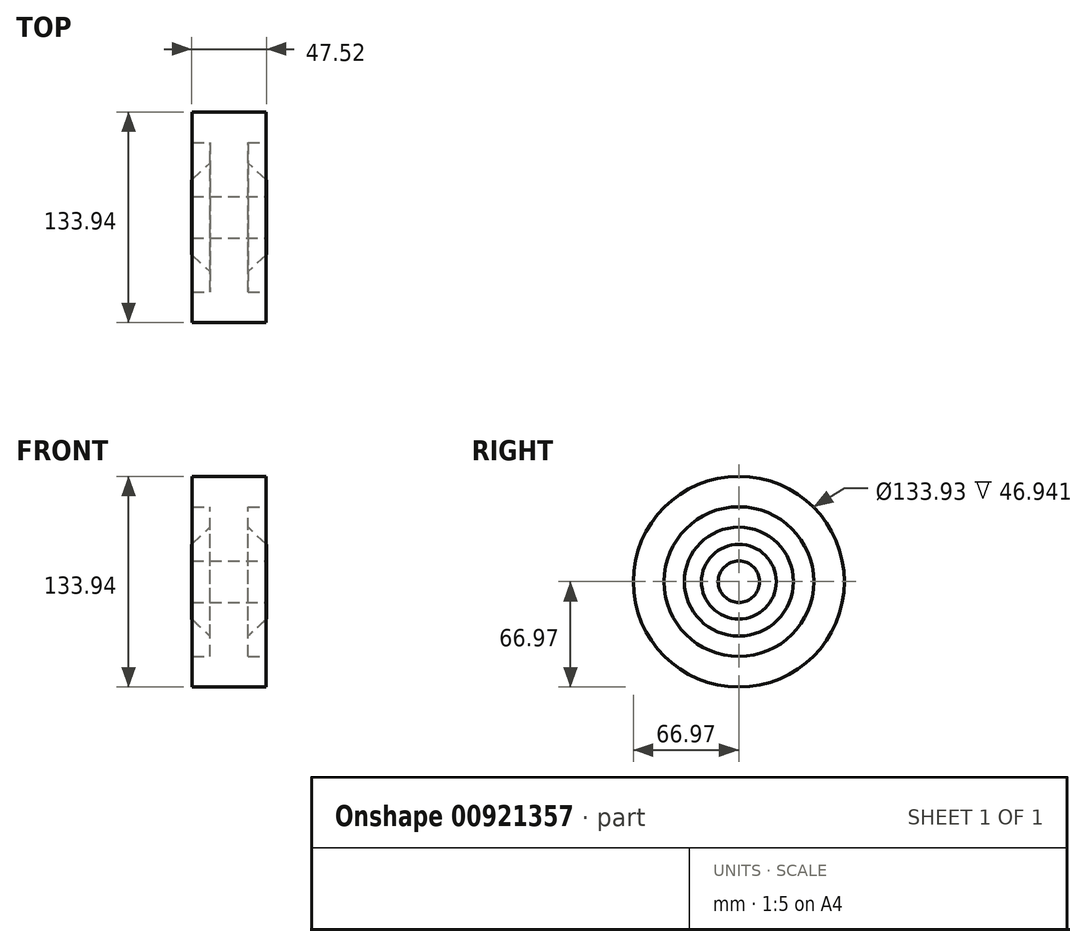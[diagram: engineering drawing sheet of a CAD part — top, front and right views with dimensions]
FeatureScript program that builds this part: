
annotation { "Feature Type Name" : "Feature", "Feature Type Description" : "" }
export const myFeature = defineFeature(function(context is Context, id is Id, definition is map)
    precondition{}
    {
        {
            var Q0;
            Q0=qCreatedBy(makeId("Front.planeOp"),FACE);
            var sketch = newSketch(context, id + "F0", { "sketchPlane" : qUnion([Q0])});
            skLineSegment(sketch, "E0", {"start": v(-23.47, 47.55) * mm, "end": v(-23.47, 66.97) * mm});
            skLineSegment(sketch, "E1", {"start": v(-23.47, 66.97) * mm, "end": v(0, 66.97) * mm});
            skLineSegment(sketch, "E2", {"start": v(-12, 47.55) * mm, "end": v(-23.47, 47.55) * mm});
            skLineSegment(sketch, "E3", {"start": v(-12, 34.6) * mm, "end": v(-12, 47.55) * mm});
            skLineSegment(sketch, "E4", {"start": v(-23.76, 23.72) * mm, "end": v(-12, 34.6) * mm});
            skLineSegment(sketch, "E5", {"start": v(-23.76, 13.13) * mm, "end": v(-23.76, 23.72) * mm});
            skLineSegment(sketch, "E6", {"start": v(0, 13.13) * mm, "end": v(-23.76, 13.13) * mm});
            skLineSegment(sketch, "E7", {"start": v(-44.36, 0) * mm, "end": v(42.73, 0) * mm});
            skLineSegment(sketch, "E8.MirrorCS", {"start": v(23.47, 66.97) * mm, "end": v(0, 66.97) * mm});
            skLineSegment(sketch, "E9.MirrorCS", {"start": v(23.47, 47.55) * mm, "end": v(23.47, 66.97) * mm});
            skLineSegment(sketch, "E10.MirrorCS", {"start": v(12, 47.55) * mm, "end": v(23.47, 47.55) * mm});
            skLineSegment(sketch, "E11.MirrorCS", {"start": v(12, 34.6) * mm, "end": v(12, 47.55) * mm});
            skLineSegment(sketch, "E12.MirrorCS", {"start": v(23.76, 23.72) * mm, "end": v(12, 34.6) * mm});
            skLineSegment(sketch, "E13.MirrorCS", {"start": v(23.76, 13.13) * mm, "end": v(23.76, 23.72) * mm});
            skLineSegment(sketch, "E14.MirrorCS", {"start": v(0, 13.13) * mm, "end": v(23.76, 13.13) * mm});
            skSolve(sketch);
        }
        {
            var Q0;
            Q0 = qSketchRegion(id + "F0", true);
            var Q1;
            Q1=sQuery(id+"F0.wireOp",EDGE,"E3");
            var Q2;
            Q2=sQuery(id+"F0.wireOp",EDGE,"E2");
            var Q3;
            Q3=sQuery(id+"F0.wireOp",EDGE,"E0");
            var Q4;
            Q4=sQuery(id+"F0.wireOp",EDGE,"E1");
            var Q5;
            Q5=sQuery(id+"F0.wireOp",EDGE,"E4");
            var Q6;
            Q6=sQuery(id+"F0.wireOp",EDGE,"E5");
            var Q7;
            Q7=sQuery(id+"F0.wireOp",EDGE,"E6");
            var Q8;
            Q8=sQuery(id+"F0.wireOp",EDGE,"E14.MirrorCS");
            var Q9;
            Q9=sQuery(id+"F0.wireOp",EDGE,"E13.MirrorCS");
            var Q10;
            Q10=sQuery(id+"F0.wireOp",EDGE,"E12.MirrorCS");
            var Q11;
            Q11=sQuery(id+"F0.wireOp",EDGE,"E11.MirrorCS");
            var Q12;
            Q12=sQuery(id+"F0.wireOp",EDGE,"E10.MirrorCS");
            var Q13;
            Q13=sQuery(id+"F0.wireOp",EDGE,"E9.MirrorCS");
            var Q14;
            Q14=sQuery(id+"F0.wireOp",EDGE,"E8.MirrorCS");
            var Q15;
            Q15=sQuery(id+"F0.wireOp",EDGE,"E7");
            revolve(context, id + "F1", {"bodyType" : ToolBodyType.SURFACE, "surfaceOperationType" : NewSurfaceOperationType.NEW, "entities" : qUnion([Q0]), "surfaceEntities" : qUnion([Q1, Q2, Q3, Q4, Q5, Q6, Q7, Q8, Q9, Q10, Q11, Q12, Q13, Q14]), "axis" : qUnion([Q15]), "revolveType" : RevolveType.FULL});
        }
    });
